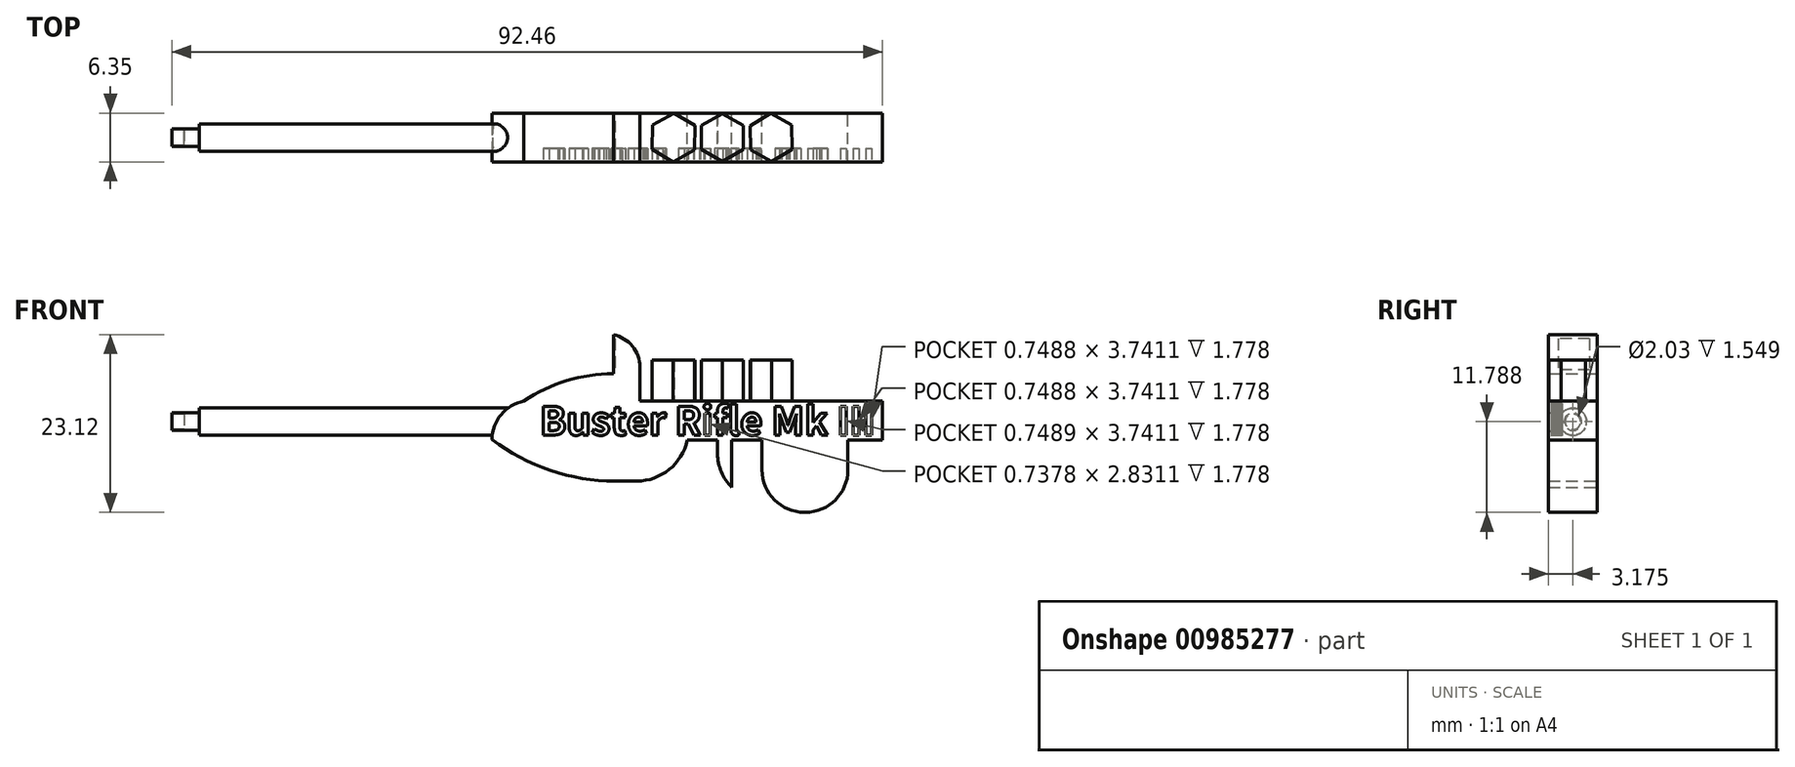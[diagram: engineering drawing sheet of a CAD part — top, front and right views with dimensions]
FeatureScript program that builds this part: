
annotation { "Feature Type Name" : "Feature", "Feature Type Description" : "" }
export const myFeature = defineFeature(function(context is Context, id is Id, definition is map)
    precondition{}
    {
        {
            var Q0;
            Q0=qCreatedBy(makeId("Front.planeOp"),FACE);
            var sketch = newSketch(context, id + "F0", { "sketchPlane" : qUnion([Q0])});
            skLineSegment(sketch, "E0.bottom", {"start": v(-19.22, 21.95) * mm, "end": v(31.58, 21.95) * mm});
            skLineSegment(sketch, "E0.top", {"start": v(-19.22, 16.87) * mm, "end": v(31.58, 16.87) * mm});
            skLineSegment(sketch, "E0.left", {"start": v(-19.22, 21.95) * mm, "end": v(-19.22, 16.87) * mm});
            skLineSegment(sketch, "E0.right", {"start": v(31.58, 21.95) * mm, "end": v(31.58, 16.87) * mm});
            skSolve(sketch);
        }
        {
            var Q0;
            Q0 = qSketchRegion(id + "F0", true);
            extrude(context, id + "F1", {"entities" : qUnion([Q0]), "depth" : 6.35 * mm, "offsetDistance" : 25.4 * mm});
        }
        {
            var Q0;
            Q0=makeQuery(id+"F1.opExtrude","SWEPT_FACE",FACE,{"disambiguationData":[OSD([sQuery(id+"F0.wireOp",EDGE,"E0.left")])]});
            var sketch = newSketch(context, id + "F2", { "sketchPlane" : qUnion([Q0])});
            skCircle(sketch, "E1", {"center": v(3.18, 19.26) * mm, "radius": 1.78 * mm});
            skPoint(sketch, "E1.centerSnap0", {"position": v(3.18, 21.95) * mm});
            skSolve(sketch);
        }
        {
            var Q0;
            Q0 = qSketchRegion(id + "F2", true);
            extrude(context, id + "F3", {"entities" : qUnion([Q0]), "operationType" : NewBodyOperationType.ADD, "depth" : 38.1 * mm, "offsetDistance" : 25.4 * mm});
        }
        {
            var Q0;
            Q0=makeQuery(id+"F3.opExtrude","CAP_FACE",FACE,{"disambiguationData":[OSD([sQuery(id+"F2.wireOp",EDGE,"E1")])],"isStart":false});
            var sketch = newSketch(context, id + "F4", { "sketchPlane" : qUnion([Q0])});
            skCircle(sketch, "E2", {"center": v(3.18, 19.26) * mm, "radius": 1.14 * mm});
            skSolve(sketch);
        }
        {
            var Q0;
            Q0 = qSketchRegion(id + "F4", true);
            extrude(context, id + "F5", {"entities" : qUnion([Q0]), "operationType" : NewBodyOperationType.ADD, "depth" : 3.56 * mm, "offsetDistance" : 25.4 * mm});
        }
        {
            var Q0;
            Q0=makeQuery(id+"F1.opExtrude","SWEPT_FACE",FACE,{"disambiguationData":[OSD([sQuery(id+"F0.wireOp",EDGE,"E0.bottom")])]});
            var sketch = newSketch(context, id + "F6", { "sketchPlane" : qUnion([Q0])});
            skLineSegment(sketch, "E3.bottom", {"start": v(-15.07, 0) * mm, "end": v(0, 0) * mm});
            skLineSegment(sketch, "E3.top", {"start": v(-15.07, -6.35) * mm, "end": v(0, -6.35) * mm});
            skLineSegment(sketch, "E3.left", {"start": v(-15.07, 0) * mm, "end": v(-15.07, -6.35) * mm});
            skLineSegment(sketch, "E3.right", {"start": v(0, 0) * mm, "end": v(0, -6.35) * mm});
            skSolve(sketch);
        }
        {
            var Q0;
            Q0 = qSketchRegion(id + "F6", true);
            extrude(context, id + "F7", {"entities" : qUnion([Q0]), "operationType" : NewBodyOperationType.ADD, "depth" : 3.56 * mm, "offsetDistance" : 25.4 * mm});
        }
        {
            var Q0;
            Q0=makeQuery(id+"F7.opExtrude","CAP_EDGE",EDGE,{"disambiguationData":[OSD([sQuery(id+"F6.wireOp",EDGE,"E3.left")])],"isStart":false});
            fillet(context, id + "F8", {"entities" : qUnion([Q0]), "radius" : 20.79 * mm, "tangentPropagation" : true, "allowEdgeOverflow" : false});
        }
        {
            var Q0;
            Q0=makeQuery(id+"F7.opExtrude","CAP_FACE",FACE,{"disambiguationData":[OSD([sQuery(id+"F6.wireOp",EDGE,"E3.bottom"),sQuery(id+"F6.wireOp",EDGE,"E3.top"),sQuery(id+"F6.wireOp",EDGE,"E3.left"),sQuery(id+"F6.wireOp",EDGE,"E3.right")])],"isStart":false});
            var sketch = newSketch(context, id + "F9", { "sketchPlane" : qUnion([Q0])});
            skLineSegment(sketch, "E4.bottom", {"start": v(0, 0) * mm, "end": v(-3.44, 0) * mm});
            skLineSegment(sketch, "E4.top", {"start": v(0, -6.35) * mm, "end": v(-3.44, -6.35) * mm});
            skLineSegment(sketch, "E4.left", {"start": v(0, 0) * mm, "end": v(0, -6.35) * mm});
            skLineSegment(sketch, "E4.right", {"start": v(-3.44, 0) * mm, "end": v(-3.44, -6.35) * mm});
            skSolve(sketch);
        }
        {
            var Q0;
            Q0 = qSketchRegion(id + "F9", true);
            extrude(context, id + "F10", {"entities" : qUnion([Q0]), "operationType" : NewBodyOperationType.ADD, "depth" : 5.08 * mm, "offsetDistance" : 25.4 * mm});
        }
        {
            var Q0;
            Q0=makeQuery(id+"F10.opExtrude","SWEPT_FACE",FACE,{"disambiguationData":[OSD([sQuery(id+"F9.wireOp",EDGE,"E4.right")])]});
            var sketch = newSketch(context, id + "F11", { "sketchPlane" : qUnion([Q0])});
            skLineSegment(sketch, "E5.bottom", {"start": v(1.02, 30.08) * mm, "end": v(5.08, 30.08) * mm});
            skLineSegment(sketch, "E5.top", {"start": v(1.02, 26.01) * mm, "end": v(5.08, 26.01) * mm});
            skLineSegment(sketch, "E5.left", {"start": v(1.02, 30.08) * mm, "end": v(1.02, 26.01) * mm});
            skLineSegment(sketch, "E5.right", {"start": v(5.08, 30.08) * mm, "end": v(5.08, 26.01) * mm});
            skPoint(sketch, "E5.middle", {"position": v(3.05, 28.05) * mm});
            skPoint(sketch, "E5.middle.positionSnap0", {"position": v(6.35, 28.05) * mm});
            skPoint(sketch, "E5.centerSnap0", {"position": v(6.35, 28.05) * mm});
            skSolve(sketch);
        }
        {
            var Q0;
            Q0 = qSketchRegion(id + "F11", true);
            extrude(context, id + "F12", {"entities" : qUnion([Q0]), "operationType" : NewBodyOperationType.REMOVE, "oppositeDirection" : true, "depth" : 0.23 * mm, "offsetDistance" : 25.4 * mm});
        }
        {
            var Q0;
            Q0=makeQuery(id+"F5.opExtrude","CAP_FACE",FACE,{"disambiguationData":[OSD([sQuery(id+"F4.wireOp",EDGE,"E2")])],"isStart":false});
            var sketch = newSketch(context, id + "F13", { "sketchPlane" : qUnion([Q0])});
            skCircle(sketch, "E6", {"center": v(3.18, 19.26) * mm, "radius": 1.01 * mm});
            skSolve(sketch);
        }
        {
            var Q0;
            Q0 = qSketchRegion(id + "F13", true);
            extrude(context, id + "F14", {"entities" : qUnion([Q0]), "operationType" : NewBodyOperationType.REMOVE, "oppositeDirection" : true, "depth" : 1.55 * mm, "offsetDistance" : 25.4 * mm});
        }
        {
            var Q0;
            {var subQ0=sQuery(id+"F0.wireOp",EDGE,"E0.right");var subQ3=sQuery(id+"F0.wireOp",EDGE,"E0.bottom");Q0=makeQuery(id+"F7.boolean.opBoolean","SPLIT",FACE,{"disambiguationData":[TD([makeQuery(id+"F1.opExtrude","SWEPT_FACE",FACE,{"disambiguationData":[OSD([subQ0])]})])],"derivedFrom":makeQuery(id+"F1.opExtrude","SWEPT_FACE",FACE,{"disambiguationData":[OSD([subQ3])]})});}
            var sketch = newSketch(context, id + "F15", { "sketchPlane" : qUnion([Q0])});
            skCircle(sketch, "E7.cCircle", {"center": v(10.75, -3.17) * mm, "radius": 2.7 * mm, "construction": true});
            skPoint(sketch, "E7.cCircle.centerSnap0", {"position": v(0, -3.18) * mm});
            skLineSegment(sketch, "E7.0", {"start": v(8.04, -4.74) * mm, "end": v(8.04, -1.61) * mm});
            skLineSegment(sketch, "E7.1", {"start": v(8.04, -1.61) * mm, "end": v(10.75, -0.05) * mm});
            skLineSegment(sketch, "E7.2", {"start": v(10.75, -0.05) * mm, "end": v(13.45, -1.61) * mm});
            skLineSegment(sketch, "E7.3", {"start": v(13.45, -1.61) * mm, "end": v(13.45, -4.74) * mm});
            skLineSegment(sketch, "E7.4", {"start": v(13.45, -4.74) * mm, "end": v(10.75, -6.3) * mm});
            skLineSegment(sketch, "E7.5", {"start": v(10.75, -6.3) * mm, "end": v(8.04, -4.74) * mm});
            skPoint(sketch, "E7.0.midPoint", {"position": v(8.04, -3.17) * mm});
            skCircle(sketch, "E8.cCircle", {"center": v(4.4, -3.18) * mm, "radius": 2.75 * mm, "construction": true});
            skLineSegment(sketch, "E8.0", {"start": v(1.67, -1.55) * mm, "end": v(4.44, 0) * mm});
            skLineSegment(sketch, "E8.1", {"start": v(4.44, 0) * mm, "end": v(7.17, -1.63) * mm});
            skLineSegment(sketch, "E8.2", {"start": v(7.17, -1.63) * mm, "end": v(7.12, -4.8) * mm});
            skLineSegment(sketch, "E8.3", {"start": v(7.12, -4.8) * mm, "end": v(4.35, -6.35) * mm});
            skLineSegment(sketch, "E8.4", {"start": v(4.35, -6.35) * mm, "end": v(1.63, -4.72) * mm});
            skLineSegment(sketch, "E8.5", {"start": v(1.63, -4.72) * mm, "end": v(1.67, -1.55) * mm});
            skPoint(sketch, "E8.0.midPoint", {"position": v(3.06, -0.78) * mm});
            skCircle(sketch, "E9.cCircle", {"center": v(17.1, -3.17) * mm, "radius": 2.72 * mm, "construction": true});
            skLineSegment(sketch, "E9.0", {"start": v(14.35, -1.65) * mm, "end": v(17.05, -0.04) * mm});
            skLineSegment(sketch, "E9.1", {"start": v(17.05, -0.04) * mm, "end": v(19.79, -1.56) * mm});
            skLineSegment(sketch, "E9.2", {"start": v(19.79, -1.56) * mm, "end": v(19.84, -4.7) * mm});
            skLineSegment(sketch, "E9.3", {"start": v(19.84, -4.7) * mm, "end": v(17.14, -6.31) * mm});
            skLineSegment(sketch, "E9.4", {"start": v(17.14, -6.31) * mm, "end": v(14.4, -4.79) * mm});
            skLineSegment(sketch, "E9.5", {"start": v(14.4, -4.79) * mm, "end": v(14.35, -1.65) * mm});
            skPoint(sketch, "E9.0.midPoint", {"position": v(15.7, -0.84) * mm});
            skSolve(sketch);
        }
        {
            var Q0;
            Q0 = qSketchRegion(id + "F15", true);
            extrude(context, id + "F16", {"entities" : qUnion([Q0]), "operationType" : NewBodyOperationType.ADD, "depth" : 5.33 * mm, "offsetDistance" : 25.4 * mm});
        }
        {
            var Q0;
            Q0=makeQuery(id+"F1.opExtrude","SWEPT_EDGE",EDGE,{"disambiguationData":[OSD([sQuery(id+"F0.wireOp",EDGE,"E0.bottom"),sQuery(id+"F0.wireOp",EDGE,"E0.left")])]});
            fillet(context, id + "F17", {"entities" : qUnion([Q0]), "radius" : 5.08 * mm, "tangentPropagation" : true, "allowEdgeOverflow" : false});
        }
        {
            var Q0;
            Q0=makeQuery(id+"F10.opExtrude","CAP_EDGE",EDGE,{"disambiguationData":[OSD([sQuery(id+"F9.wireOp",EDGE,"E4.left")])],"isStart":false});
            fillet(context, id + "F18", {"entities" : qUnion([Q0]), "radius" : 4.3 * mm, "tangentPropagation" : true, "allowEdgeOverflow" : false});
        }
        {
            var Q0;
            Q0=makeQuery(id+"F1.opExtrude","SWEPT_FACE",FACE,{"disambiguationData":[OSD([sQuery(id+"F0.wireOp",EDGE,"E0.top")])]});
            var sketch = newSketch(context, id + "F19", { "sketchPlane" : qUnion([Q0])});
            skLineSegment(sketch, "E10.bottom", {"start": v(-19.22, 6.35) * mm, "end": v(6.18, 6.35) * mm});
            skLineSegment(sketch, "E10.top", {"start": v(-19.22, 0) * mm, "end": v(6.18, 0) * mm});
            skLineSegment(sketch, "E10.left", {"start": v(-19.22, 6.35) * mm, "end": v(-19.22, 0) * mm});
            skLineSegment(sketch, "E10.right", {"start": v(6.18, 6.35) * mm, "end": v(6.18, 0) * mm});
            skSolve(sketch);
        }
        {
            var Q0;
            Q0 = qSketchRegion(id + "F19", true);
            extrude(context, id + "F20", {"entities" : qUnion([Q0]), "operationType" : NewBodyOperationType.ADD, "depth" : 5.33 * mm, "offsetDistance" : 25.4 * mm});
        }
        {
            var Q0;
            Q0=makeQuery(id+"F20.opExtrude","CAP_EDGE",EDGE,{"disambiguationData":[OSD([sQuery(id+"F19.wireOp",EDGE,"E10.right")])],"isStart":false});
            fillet(context, id + "F21", {"entities" : qUnion([Q0]), "radius" : 6.75 * mm, "tangentPropagation" : true, "allowEdgeOverflow" : false});
        }
        {
            var Q0;
            Q0=makeQuery(id+"F20.opExtrude","CAP_EDGE",EDGE,{"disambiguationData":[OSD([sQuery(id+"F19.wireOp",EDGE,"E10.left")])],"isStart":false});
            fillet(context, id + "F22", {"entities" : qUnion([Q0]), "radius" : 26.37 * mm, "tangentPropagation" : true, "allowEdgeOverflow" : false});
        }
        {
            var Q0;
            Q0=makeQuery(id+"F1.opExtrude","SWEPT_FACE",FACE,{"disambiguationData":[OSD([sQuery(id+"F0.wireOp",EDGE,"E0.top")])]});
            var sketch = newSketch(context, id + "F23", { "sketchPlane" : qUnion([Q0])});
            skLineSegment(sketch, "E11.bottom", {"start": v(15.9, 6.35) * mm, "end": v(27.08, 6.35) * mm});
            skLineSegment(sketch, "E11.top", {"start": v(15.9, 0) * mm, "end": v(27.08, 0) * mm});
            skLineSegment(sketch, "E11.left", {"start": v(15.9, 6.35) * mm, "end": v(15.9, 0) * mm});
            skLineSegment(sketch, "E11.right", {"start": v(27.08, 6.35) * mm, "end": v(27.08, 0) * mm});
            skPoint(sketch, "E11.middle", {"position": v(21.5, 3.18) * mm});
            skPoint(sketch, "E11.middle.positionSnap0", {"position": v(6.18, 3.18) * mm});
            skPoint(sketch, "E11.centerSnap0", {"position": v(6.18, 3.18) * mm});
            skSolve(sketch);
        }
        {
            var Q0;
            Q0 = qSketchRegion(id + "F23", true);
            extrude(context, id + "F24", {"entities" : qUnion([Q0]), "operationType" : NewBodyOperationType.ADD, "depth" : 9.4 * mm, "offsetDistance" : 25.4 * mm});
        }
        {
            var Q0;
            {var subQ2=sQuery(id+"F0.wireOp",EDGE,"E0.top");Q0=makeQuery(id+"F24.boolean.opBoolean","SPLIT",FACE,{"disambiguationData":[TD([makeQuery(id+"F21.opFillet","BLEND_FACE",FACE,{"disambiguationData":[OSD([sQuery(id+"F19.wireOp",EDGE,"E10.right")])]})])],"derivedFrom":makeQuery(id+"F1.opExtrude","SWEPT_FACE",FACE,{"disambiguationData":[OSD([subQ2])]})});}
            var sketch = newSketch(context, id + "F25", { "sketchPlane" : qUnion([Q0])});
            skLineSegment(sketch, "E12.bottom", {"start": v(10.12, 6.35) * mm, "end": v(11.96, 6.35) * mm});
            skLineSegment(sketch, "E12.top", {"start": v(10.12, 0) * mm, "end": v(11.96, 0) * mm});
            skLineSegment(sketch, "E12.left", {"start": v(10.12, 6.35) * mm, "end": v(10.12, 0) * mm});
            skLineSegment(sketch, "E12.right", {"start": v(11.96, 6.35) * mm, "end": v(11.96, 0) * mm});
            skPoint(sketch, "E12.middle", {"position": v(11.04, 3.17) * mm});
            skPoint(sketch, "E12.middle.positionSnap0", {"position": v(11.04, 0) * mm});
            skPoint(sketch, "E12.centerSnap0", {"position": v(11.04, 0) * mm});
            skSolve(sketch);
        }
        {
            var Q0;
            Q0 = qSketchRegion(id + "F25", true);
            extrude(context, id + "F26", {"entities" : qUnion([Q0]), "operationType" : NewBodyOperationType.ADD, "depth" : 6.15 * mm, "offsetDistance" : 25.4 * mm});
        }
        {
            var Q0;
            Q0=makeQuery(id+"F26.opExtrude","CAP_EDGE",EDGE,{"disambiguationData":[OSD([sQuery(id+"F25.wireOp",EDGE,"E12.left")])],"isStart":false});
            fillet(context, id + "F27", {"entities" : qUnion([Q0]), "radius" : 6.13 * mm, "tangentPropagation" : true, "allowEdgeOverflow" : false});
        }
        {
            var Q0;
            Q0=makeQuery(id+"F26.boolean.opBoolean","MERGE",FACE,{"derivedFrom":[makeQuery(id+"F24.boolean.opBoolean","MERGE",FACE,{"derivedFrom":[makeQuery(id+"F20.boolean.opBoolean","MERGE",FACE,{"derivedFrom":[makeQuery(id+"F10.boolean.opBoolean","MERGE",FACE,{"derivedFrom":[makeQuery(id+"F7.boolean.opBoolean","MERGE",FACE,{"derivedFrom":[makeQuery(id+"F1.opExtrude","CAP_FACE",FACE,{"disambiguationData":[OSD([sQuery(id+"F0.wireOp",EDGE,"E0.bottom"),sQuery(id+"F0.wireOp",EDGE,"E0.top"),sQuery(id+"F0.wireOp",EDGE,"E0.left"),sQuery(id+"F0.wireOp",EDGE,"E0.right")])],"isStart":false}),makeQuery(id+"F7.opExtrude","SWEPT_FACE",FACE,{"disambiguationData":[OSD([sQuery(id+"F6.wireOp",EDGE,"E3.top")])]})]}),makeQuery(id+"F10.opExtrude","SWEPT_FACE",FACE,{"disambiguationData":[OSD([sQuery(id+"F9.wireOp",EDGE,"E4.top")])]})]}),makeQuery(id+"F20.opExtrude","SWEPT_FACE",FACE,{"disambiguationData":[OSD([sQuery(id+"F19.wireOp",EDGE,"E10.bottom")])]})]}),makeQuery(id+"F24.opExtrude","SWEPT_FACE",FACE,{"disambiguationData":[OSD([sQuery(id+"F23.wireOp",EDGE,"E11.bottom")])]})]}),makeQuery(id+"F26.opExtrude","SWEPT_FACE",FACE,{"disambiguationData":[OSD([sQuery(id+"F25.wireOp",EDGE,"E12.bottom")])]})]});
            var sketch = newSketch(context, id + "F28", { "sketchPlane" : qUnion([Q0])});
            skText(sketch, "E13", { "text": "Buster Rifle Mk III", "fontName": "NotoSansCJKjp-Bold.otf"});
            const initialGuessF28  = {"E13": [-0.013, 0.01753, 1, 0, 0.00364]};
            skSetInitialGuess(sketch, initialGuessF28);
            skSolve(sketch);
        }
        {
            var Q0;
            Q0 = qSketchRegion(id + "F28", true);
            extrude(context, id + "F29", {"entities" : qUnion([Q0]), "operationType" : NewBodyOperationType.REMOVE, "oppositeDirection" : true, "depth" : 1.78 * mm, "offsetDistance" : 25.4 * mm});
        }
        {
            var Q0;
            Q0=makeQuery(id+"F24.opExtrude","CAP_EDGE",EDGE,{"disambiguationData":[OSD([sQuery(id+"F23.wireOp",EDGE,"E11.right")])],"isStart":false});
            var Q1;
            Q1=makeQuery(id+"F24.opExtrude","CAP_EDGE",EDGE,{"disambiguationData":[OSD([sQuery(id+"F23.wireOp",EDGE,"E11.left")])],"isStart":false});
            fillet(context, id + "F30", {"entities" : qUnion([Q0, Q1]), "radius" : 5.52 * mm, "tangentPropagation" : true, "allowEdgeOverflow" : false});
        }
    });
